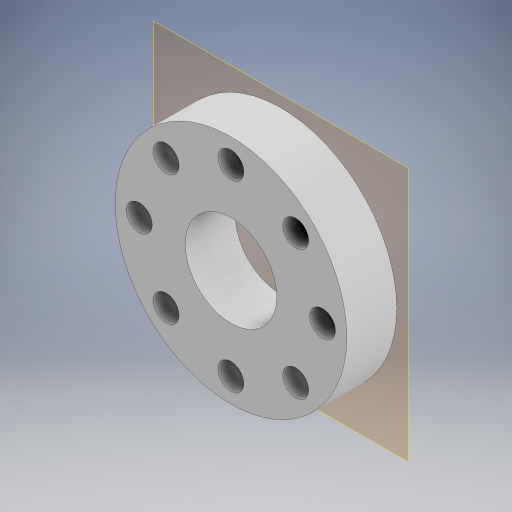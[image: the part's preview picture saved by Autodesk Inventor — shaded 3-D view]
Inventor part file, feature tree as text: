
AUTODESK INVENTOR PART (.ipt)
format: ipt  version: 2024 (Build 280153000, 153)  size: 286,720 bytes
history: native  units: in
note: dims shown in document units (in); Inventor stores cm internally (conversion verified against a paired STEP export)
features: other x4, extrude x1, sketch x1, reference x1
ambient origin geometry x8: Origin, YZ Plane, XZ Plane, XY Plane, X Axis, Y Axis, Z Axis, Center Point
bodies: Body1 (feature_tree)
feature tree (7):
  other  "솔리드1"
  other  "작업 평면1"
  extrude  "돌출1"  Depth=0.0197in
  sketch  "스케치1"
  reference  "참조1"
  other  "조립품17"
  other  "64-106Horn:1"
